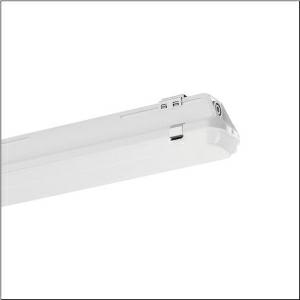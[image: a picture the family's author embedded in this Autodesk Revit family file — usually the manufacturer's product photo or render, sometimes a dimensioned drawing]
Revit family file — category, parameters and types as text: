
# Revit family: monsun_r__11_51fp10dp480l_6cbf
name_source: partatom
category: Lighting Fixtures
units: mm (PartAtom-declared; Revit-internal decimal feet)

## family parameters
Cut with Voids When Loaded = No
Host = Face
Light Source = No
Part Type = Normal
Room Calculation Point = No
Round Connector Dimension = Use Diameter
Shared = No

## types (1)
- --- (1 x LED, 8000 lm, 44.4 W, 4000K)
    Apparent Load = 44 VA
    CIE Flux Codes = 47 77 93 94 100
    Color Rendering = 80
    Color Temperature = 4000K
    Default Elevation = 1800 mm
    Description = Monsun® 11, damp-proof luminaire, chain hanger, primary optical cover: enclosure, of PMMA, light emission: direct distribution, primary light characteristic: symmetric, installation type: suspended mounting, surface-mounted, horizontal mounting, vertical mounting, LED, rated luminous flux: 8.000lm, luminous efficacy: 180lm/W, light colour: 840, colour temperature: 4000K, control gear: DALI 2, with terminal, 5-pole, max. 2.5mm², mains connection: 220..240V, AC, 50/60Hz, rated input power: 44W, luminaire housing, of glass-fibre reinforced polyester, uncoated, bright grey, incl. chain hanger, length: 1.590mm, width: 90mm, height: 88mm, clip for enclosure, of stainless steel (V2A), ceiling mounting element, of stainless steel (V2A), chain hanger, of stainless steel (V2A), protection rating (complete): IP66, insulation class (complete): insulation class I (protective earthing), certification: CE, ENEC, VDE, UKCA, protection symbol: D, impact resistance: IK04, permissible operating ambient temperature: -25..+40°C, standard: EN 50419, EN 60598-2-1, corresponds to IFS (International Featured Standards) requirements for safety and quality in the food industry, for indoor or canopied outdoor use, no direct snow, no direct sun, no direct rain, LABS conformity tested according to VDMA 24364:2018-05, contact your sales advisor before using the luminaires in applications with unclear chemical exposure, large temperature fluctuations or condensation-forming humidity, packaging unit: 1 piece
    Height = 89 mm
    Lamp = 1 x LED
    Lamp Light Flux = 8000 lm
    Lamp Power = 44.4 W
    Lamp count = 1
    Length = 1590 mm
    Luminous efficacy = 180 lm/W
    Manufacturer = Siteco
    ModVariant = No
    Model = 51FP10DP480L
    Mounting Place = Ceiling
    Mounting Type = Surface mounted
    Number of Poles = 1
    OnlyDefault = Yes
    Power Factor = 1
    Product Name = Monsun® 11
    Product group = damp-proof luminaire
    ProductGroupID = 301
    Protection Class = Protection class I
    Protection Degree = IP 66
    RLX_Detail_Level = 1
    RLX_Emergency_Light_Flux = 0 lm
    RLX_Emergency_Type = 0
    RLX_Emergency_Type_DB = No
    RlxData = <blob elided: 92149 chars, md5=ee81705c>
    Socket = socket
    Standby Power = 0 W
    System Light Flux = 8000 lm
    System Power = 44 W
    Type Comments = factory setting: luminous flux: 100 % | dim-lin: 254 | 295 mA
    Type Image = l_1349237.jpg
    URL = http://relux.com
    VarID = @adj_038005
    Voltage = 0 V
    Weight = 0.00 kg
    Width = 90 mm

## geometry (parser evidence)
native form markers: Blend x4, Sweep x12
no freeform markers — native parametric forms only
